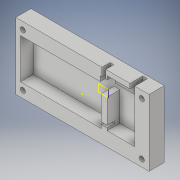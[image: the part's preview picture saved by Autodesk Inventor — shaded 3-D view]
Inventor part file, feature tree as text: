
AUTODESK INVENTOR PART (.ipt)
format: ipt  version: 2018 (Build 220112000, 112)  size: 256,512 bytes
history: native  units: in
note: dims shown in document units (in); Inventor stores cm internally (conversion verified against a paired STEP export)
features: extrude x10, sketch x7, plane x4, projected_geometry x4, hole x2
ambient origin geometry x8: Origin, YZ Plane, XZ Plane, XY Plane, X Axis, Y Axis, Z Axis, Center Point
bodies: Solid1 (feature_tree)
feature tree (27):
  extrude  "Extrusion1"  Depth=3.5in
  extrude  "Extrusion2"  Depth=2.105in
  extrude  "Extrusion4"  Depth=0.25in
  plane  "Work Plane1"
  plane  "Work Plane2"
  extrude  "Extrusion5"  Depth=0.38in
  plane  "Work Plane3"
  plane  "Work Plane4"
  sketch  "Sketch6"  dims[d4=0.25in d5=4.075in]
  extrude  "Extrusion6"  Depth=0.675in
  extrude  "Extrusion7"  Depth=0.2in
  extrude  "Extrusion8"  Depth=0.125in TaperAngle=0.0deg
  extrude  "Extrusion9"  Depth=0.0625in
  extrude  "Extrusion10"  Depth=0.25in
  hole  "Hole2"  [1 undecoded]
  extrude  "Extrusion11"  Depth=2.0in
  sketch  "Sketch3"  dims[d0=7.0in d1=3.5in]
  projected_geometry  "Projected Loop2"
  sketch  "Sketch5"  dims[d2=4.25in d3=2.105in]
  projected_geometry  "Projected Loop3"
  sketch  "Sketch7"  dims[d7=0.33in d8=0.38in]
  projected_geometry  "Projected Loop4"
  sketch  "Sketch8"  dims[d9=0.675in d10=0.0in d13=0.525in]
  sketch  "Sketch9"  dims[d15=0.2in d17=0.4in]
  hole  "Hole1"  [1 undecoded]
  sketch  "Sketch10"  dims[d18=0.5in d19=0.0in d22=0.125in d23=0.0in d24=0.0625in d25=0.22in d26=1.45in d27=2.0in d28=0.75in d29=0.25in d30=0.125in d31=0.0in d32=0.5in d33=0.125in d34=0.125in d35=0.875in d36=0.375in d37=0.0in d38=0.375in d39=0.0in d40=0.25in d41=0.0in d42=0.25in d43=0.0in d44=0.25in d45=0.0in d46=0.266in d47=0.75in d48=0.375in d49=0.25in d50=0.5635in d51=1.0in d52=0.0in d53=0.25in d54=0.0in]
  projected_geometry  "Projected Loop5"
note: 2 required parameter values undecoded (feature->parameter linkage not recoverable at this tier; creation-order binding heuristic only, values carry confidence <= 0.55)
